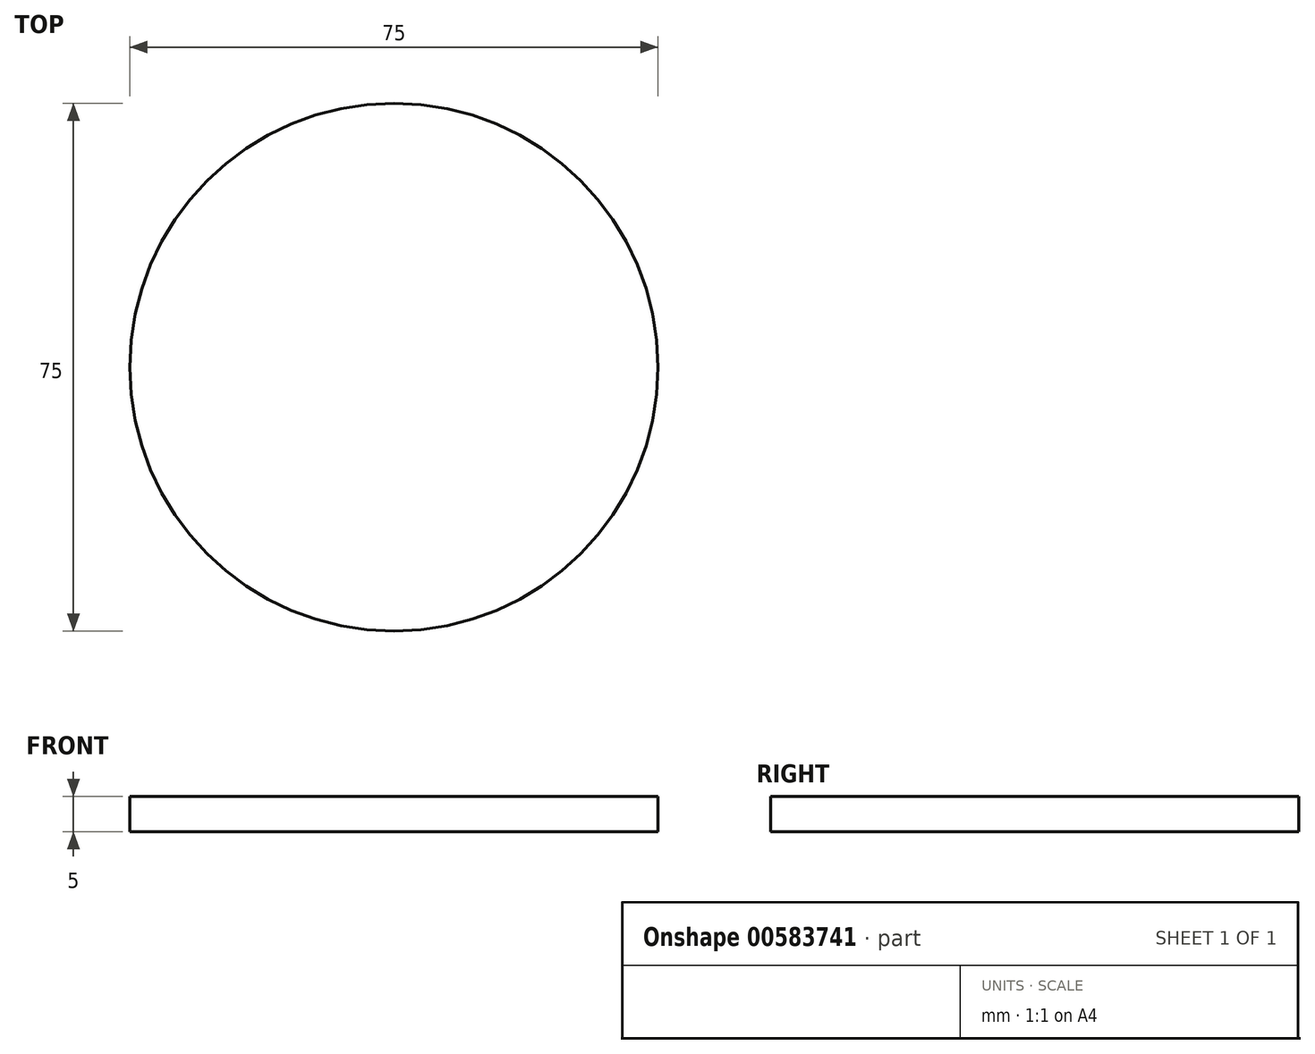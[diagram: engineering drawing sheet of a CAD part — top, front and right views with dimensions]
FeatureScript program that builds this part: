
annotation { "Feature Type Name" : "Feature", "Feature Type Description" : "" }
export const myFeature = defineFeature(function(context is Context, id is Id, definition is map)
    precondition{}
    {
        {
            var Q0;
            Q0=qCreatedBy(makeId("Top.planeOp"),FACE);
            var sketch = newSketch(context, id + "F0", { "sketchPlane" : qUnion([Q0])});
            skCircle(sketch, "E0", {"center": v(0, 0) * mm, "radius": 37.5 * mm});
            skSolve(sketch);
        }
        {
            var Q0;
            Q0=makeQuery(id+"F0.imprint","IMPRINT",FACE,{"disambiguationData":[TD([[makeQuery(id+"F0.imprint","IMPRINT",EDGE,{"derivedFrom":sQuery(id+"F0.wireOp",EDGE,"E0")}),1.0]])]});
            extrude(context, id + "F1", {"entities" : qUnion([Q0]), "depth" : 5 * mm, "offsetDistance" : 25 * mm});
        }
    });
